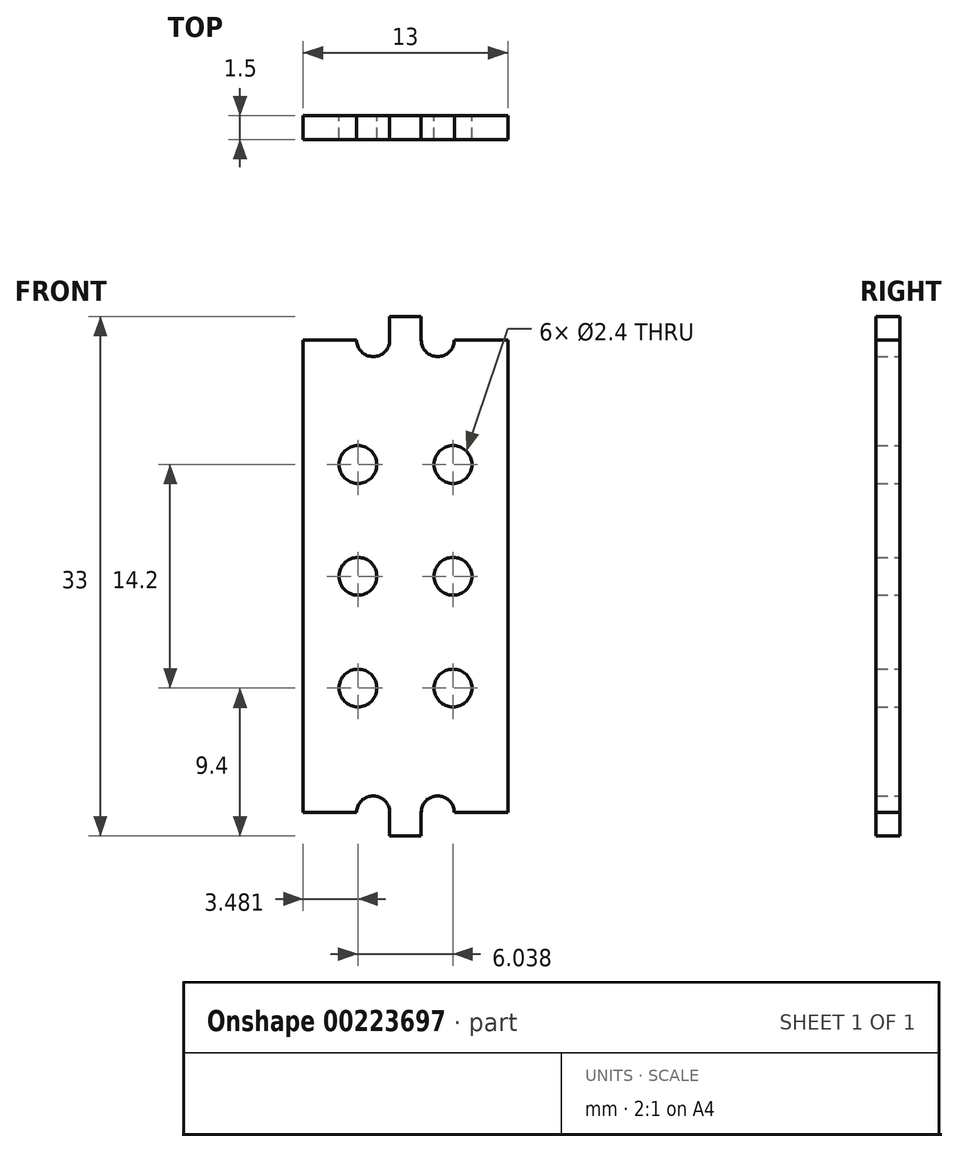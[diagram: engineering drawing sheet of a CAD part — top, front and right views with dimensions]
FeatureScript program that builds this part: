
annotation { "Feature Type Name" : "Feature", "Feature Type Description" : "" }
export const myFeature = defineFeature(function(context is Context, id is Id, definition is map)
    precondition{}
    {
        {
            var Q0;
            Q0=qCreatedBy(makeId("Front.planeOp"),FACE);
            var sketch = newSketch(context, id + "F0", { "sketchPlane" : qUnion([Q0])});
            skLineSegment(sketch, "E0.bottom", {"start": v(-3.1, 15) * mm, "end": v(-6.5, 15) * mm});
            skLineSegment(sketch, "E0.right", {"start": v(-6.5, 15) * mm, "end": v(-6.5, 0) * mm});
            skLineSegment(sketch, "E1.right", {"start": v(-1, 15) * mm, "end": v(-1, 16.5) * mm});
            skLineSegment(sketch, "E2.MirrorCS", {"start": v(6.5, 15) * mm, "end": v(6.5, 0) * mm});
            skLineSegment(sketch, "E3.MirrorCS", {"start": v(1, 15) * mm, "end": v(1, 16.5) * mm});
            skLineSegment(sketch, "E4.MirrorCS", {"start": v(3.1, 15) * mm, "end": v(6.5, 15) * mm});
            skPoint(sketch, "E0.left.start.orphan", {"position": v(0, 15) * mm});
            skCircle(sketch, "E5.MirrorC", {"center": v(3.02, 7.1) * mm, "radius": 1.2 * mm});
            skCircle(sketch, "E6.MirrorC", {"center": v(3.02, 0) * mm, "radius": 1.2 * mm});
            skArc(sketch, "E7", {"start": v(1, 15) * mm, "mid": v(2.05, 13.95) * mm, "end": v(3.1, 15) * mm});
            skArc(sketch, "E8", {"start": v(-3.1, 15) * mm, "mid": v(-2.05, 13.95) * mm, "end": v(-1, 15) * mm});
            skLineSegment(sketch, "E9", {"start": v(0, 0) * mm, "end": v(9.79, 0) * mm, "construction": true});
            skLineSegment(sketch, "E10", {"start": v(0, 0) * mm, "end": v(0, 23.02) * mm, "construction": true});
            skLineSegment(sketch, "E11", {"start": v(-1, 16.5) * mm, "end": v(1, 16.5) * mm});
            skLineSegment(sketch, "E12", {"start": v(0, 0) * mm, "end": v(-12.41, 0) * mm, "construction": true});
            skPoint(sketch, "E12.endSnap0", {"position": v(-6.5, 0) * mm});
            skLineSegment(sketch, "E13.MirrorCS", {"start": v(6.5, -15) * mm, "end": v(6.5, 0) * mm});
            skLineSegment(sketch, "E14.MirrorCS", {"start": v(-6.5, -15) * mm, "end": v(-6.5, 0) * mm});
            skLineSegment(sketch, "E15.MirrorCS", {"start": v(1, -15) * mm, "end": v(1, -16.5) * mm});
            skLineSegment(sketch, "E16.MirrorCS", {"start": v(-1, -15) * mm, "end": v(-1, -16.5) * mm});
            skPoint(sketch, "E17.MirrorP", {"position": v(0, -15) * mm});
            skLineSegment(sketch, "E18.MirrorCS", {"start": v(3.1, -15) * mm, "end": v(6.5, -15) * mm});
            skLineSegment(sketch, "E19.MirrorCS", {"start": v(-3.1, -15) * mm, "end": v(-6.5, -15) * mm});
            skLineSegment(sketch, "E20.MirrorCS", {"start": v(-1, -16.5) * mm, "end": v(1, -16.5) * mm});
            skArc(sketch, "E21.MirrorCS", {"start": v(-3.1, -15) * mm, "mid": v(-2.05, -13.95) * mm, "end": v(-1, -15) * mm});
            skArc(sketch, "E22.MirrorCS", {"start": v(1, -15) * mm, "mid": v(2.05, -13.95) * mm, "end": v(3.1, -15) * mm});
            skLineSegment(sketch, "E23", {"start": v(3.02, 11.59) * mm, "end": v(3.02, -11.22) * mm, "construction": true});
            skCircle(sketch, "E24.MirrorC", {"center": v(3.02, -7.1) * mm, "radius": 1.2 * mm});
            skCircle(sketch, "E25.MirrorC", {"center": v(-3.02, -7.1) * mm, "radius": 1.2 * mm});
            skCircle(sketch, "E26.MirrorC", {"center": v(-3.02, 0) * mm, "radius": 1.2 * mm});
            skCircle(sketch, "E27.MirrorC", {"center": v(-3.02, 7.1) * mm, "radius": 1.2 * mm});
            skSolve(sketch);
        }
        {
            var Q0;
            Q0=qSketchRegion(id+"F0",true);
            extrude(context, id + "F1", {"entities" : qUnion([Q0]), "depth" : 1.5 * mm});
        }
    });
